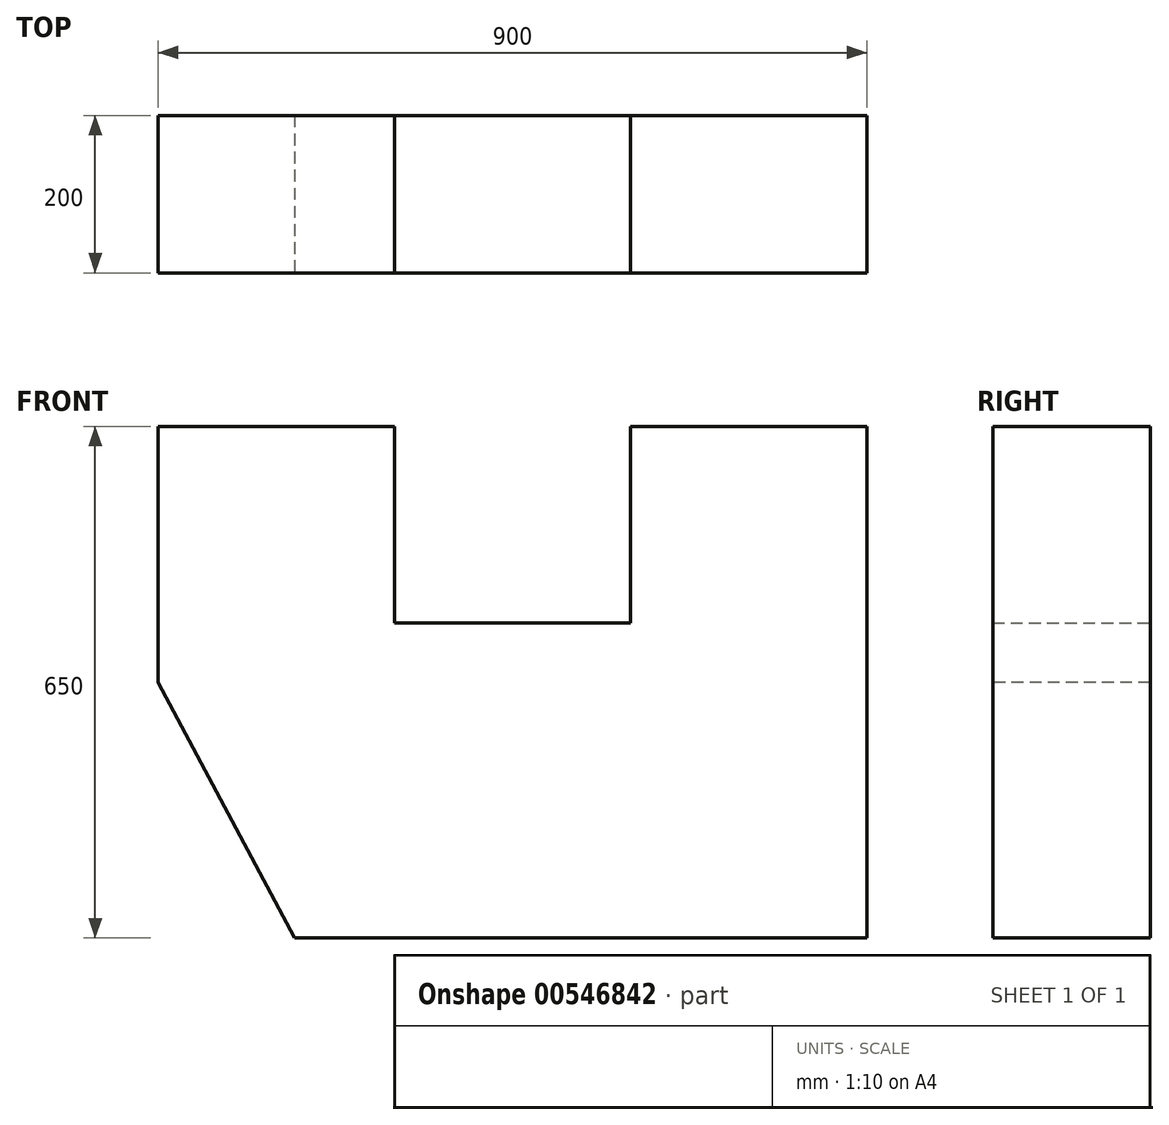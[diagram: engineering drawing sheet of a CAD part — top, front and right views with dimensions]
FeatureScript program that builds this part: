
annotation { "Feature Type Name" : "Feature", "Feature Type Description" : "" }
export const myFeature = defineFeature(function(context is Context, id is Id, definition is map)
    precondition{}
    {
        {
            var Q0;
            Q0=qCreatedBy(makeId("Front.planeOp"),FACE);
            var sketch = newSketch(context, id + "F0", { "sketchPlane" : qUnion([Q0])});
            skLineSegment(sketch, "E0.bottom", {"start": v(-301.49, 391.7) * mm, "end": v(-1.49, 391.7) * mm});
            skLineSegment(sketch, "E0.top", {"start": v(-301.49, -258.3) * mm, "end": v(598.51, -258.3) * mm});
            skLineSegment(sketch, "E0.left", {"start": v(-301.49, 391.7) * mm, "end": v(-301.49, -258.3) * mm});
            skLineSegment(sketch, "E0.right", {"start": v(598.51, 391.7) * mm, "end": v(598.51, -258.3) * mm});
            skLineSegment(sketch, "E1", {"start": v(-301.49, -258.3) * mm, "end": v(-190.92, -258.3) * mm});
            skLineSegment(sketch, "E2", {"start": v(598.51, -258.3) * mm, "end": v(-80.4, -258.3) * mm});
            skLineSegment(sketch, "E3", {"start": v(598.51, -237.83) * mm, "end": v(598.51, -258.3) * mm});
            skLineSegment(sketch, "E4.top", {"start": v(298.51, 141.7) * mm, "end": v(-1.49, 141.7) * mm});
            skLineSegment(sketch, "E4.left", {"start": v(298.51, 391.7) * mm, "end": v(298.51, 141.7) * mm});
            skLineSegment(sketch, "E4.right", {"start": v(-1.49, 391.7) * mm, "end": v(-1.49, 141.7) * mm});
            skPoint(sketch, "E4.middle", {"position": v(148.51, 391.7) * mm});
            skPoint(sketch, "E5.orphan", {"position": v(-1.49, 641.7) * mm});
            skPoint(sketch, "E6.orphan", {"position": v(298.51, 641.7) * mm});
            skLineSegment(sketch, "E7.trimOffspring", {"start": v(298.51, 391.7) * mm, "end": v(598.51, 391.7) * mm});
            skSolve(sketch);
        }
        {
            var Q0;
            Q0=makeQuery(id+"F0.imprint","IMPRINT",FACE,{"disambiguationData":[TD([[makeQuery(id+"F0.imprint","IMPRINT",EDGE,{"derivedFrom":sQuery(id+"F0.wireOp",EDGE,"E0.bottom")}),-1.0]])]});
            extrude(context, id + "F1", {"entities" : qUnion([Q0]), "depth" : 200 * mm, "offsetDistance" : 25 * mm});
        }
        {
            var Q0;
            Q0=makeQuery(id+"F1.opExtrude","CAP_FACE",FACE,{"disambiguationData":[OSD([sQuery(id+"F0.wireOp",EDGE,"E0.bottom"),sQuery(id+"F0.wireOp",EDGE,"E0.top"),sQuery(id+"F0.wireOp",EDGE,"E0.left"),sQuery(id+"F0.wireOp",EDGE,"E0.right"),sQuery(id+"F0.wireOp",EDGE,"E1"),sQuery(id+"F0.wireOp",EDGE,"E2"),sQuery(id+"F0.wireOp",EDGE,"E3"),sQuery(id+"F0.wireOp",EDGE,"E4.top"),sQuery(id+"F0.wireOp",EDGE,"E4.left"),sQuery(id+"F0.wireOp",EDGE,"E4.right"),sQuery(id+"F0.wireOp",EDGE,"E7.trimOffspring")])],"isStart":false});
            var sketch = newSketch(context, id + "F2", { "sketchPlane" : qUnion([Q0])});
            skLineSegment(sketch, "E8", {"start": v(-301.49, -258.3) * mm, "end": v(-128.44, -258.3) * mm});
            skLineSegment(sketch, "E9", {"start": v(-128.44, -258.3) * mm, "end": v(-301.49, 66.7) * mm});
            skLineSegment(sketch, "E10", {"start": v(-301.49, 66.7) * mm, "end": v(-301.49, -258.3) * mm});
            skLineSegment(sketch, "E11", {"start": v(598.51, -258.3) * mm, "end": v(442.31, -258.3) * mm});
            skLineSegment(sketch, "E12", {"start": v(442.31, -258.3) * mm, "end": v(598.51, 30.4) * mm});
            skLineSegment(sketch, "E13", {"start": v(598.51, 30.4) * mm, "end": v(598.51, -258.3) * mm});
            skLineSegment(sketch, "E14", {"start": v(442.31, -258.3) * mm, "end": v(598.51, -258.3) * mm});
            skSolve(sketch);
        }
        {
            var Q0;
            {var subQ0=sQuery(id+"F2.wireOp",EDGE,"E9");Q0=makeQuery(id+"F2.imprint","IMPRINT",FACE,{"disambiguationData":[TD([[makeQuery(id+"F2.imprint","IMPRINT",EDGE,{"derivedFrom":subQ0}),-1.0]])]});}
            var sketch = newSketch(context, id + "F3", { "sketchPlane" : qUnion([Q0])});
            skSolve(sketch);
        }
        {
            var Q0;
            Q0 = qSketchRegion(id + "F3", true);
            var Q1;
            Q1=makeQuery(id+"F2.imprint","IMPRINT",FACE,{"disambiguationData":[TD([[makeQuery(id+"F2.imprint","IMPRINT",EDGE,{"derivedFrom":sQuery(id+"F2.wireOp",EDGE,"E8")}),1.0]])]});
            extrude(context, id + "F4", {"entities" : qUnion([Q0, Q1]), "operationType" : NewBodyOperationType.REMOVE, "oppositeDirection" : true, "depth" : 25 * mm, "offsetDistance" : 25 * mm});
        }
        {
            var Q0;
            Q0=makeQuery(id+"F4.boolean.opBoolean","COPY",FACE,{"derivedFrom":makeQuery(id+"F4.opExtrude","CAP_FACE",FACE,{"disambiguationData":[OSD([sQuery(id+"F2.wireOp",EDGE,"E8"),sQuery(id+"F2.wireOp",EDGE,"E9"),sQuery(id+"F2.wireOp",EDGE,"E10")])],"isStart":false})});
            extrude(context, id + "F5", {"entities" : qUnion([Q0]), "operationType" : NewBodyOperationType.REMOVE, "oppositeDirection" : true, "depth" : 400 * mm, "offsetDistance" : 25 * mm});
        }
    });
